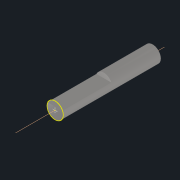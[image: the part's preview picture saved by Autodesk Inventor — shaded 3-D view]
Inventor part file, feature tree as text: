
AUTODESK INVENTOR PART (.ipt)
format: ipt  version: 2021.1 (Build 251245000, 245)  size: 83,456 bytes
history: native  units: in
note: dims shown in document units (in); Inventor stores cm internally (conversion verified against a paired STEP export)
features: extrude x2, sketch x2, projected_geometry x1
ambient origin geometry x8: Origin, YZ Plane, XZ Plane, XY Plane, X Axis, Y Axis, Z Axis, Center Point
bodies: Solid1 (feature_tree)
feature tree (5):
  extrude  "Extrusion1"  Depth=1.1811in TaperAngle=0.0deg
  extrude  "Extrusion2"  Depth=0.5906in TaperAngle=0.0deg
  sketch  "Sketch1"  dims[d0=0.1969in d1=1.1811in d2=0.0in]
  sketch  "Sketch2"  dims[d3=0.0394in d4=0.5906in d5=0.0in]
  projected_geometry  "Projected Loop1"
